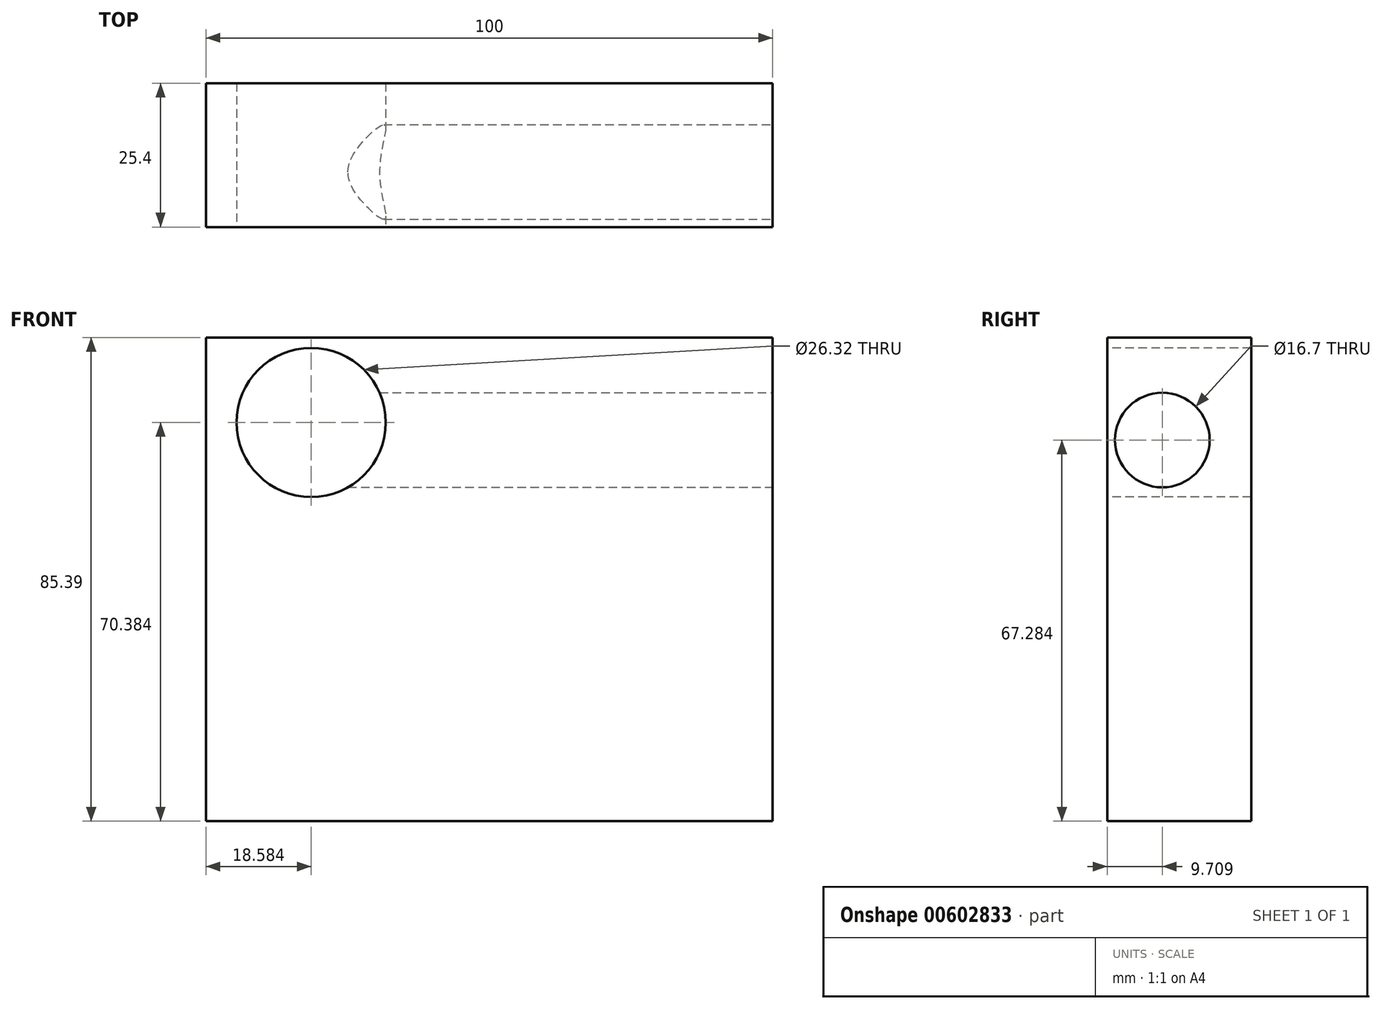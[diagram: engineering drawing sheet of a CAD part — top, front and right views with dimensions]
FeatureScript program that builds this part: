
annotation { "Feature Type Name" : "Feature", "Feature Type Description" : "" }
export const myFeature = defineFeature(function(context is Context, id is Id, definition is map)
    precondition{}
    {
        {
            var Q0;
            Q0=qCreatedBy(makeId("Front.planeOp"),FACE);
            var sketch = newSketch(context, id + "F0", { "sketchPlane" : qUnion([Q0])});
            skLineSegment(sketch, "E0.bottom", {"start": v(0, 0) * mm, "end": v(100, 0) * mm});
            skLineSegment(sketch, "E0.top", {"start": v(0, 85.4) * mm, "end": v(100, 85.4) * mm});
            skLineSegment(sketch, "E0.left", {"start": v(0, 0) * mm, "end": v(0, 85.4) * mm});
            skLineSegment(sketch, "E0.right", {"start": v(100, 0) * mm, "end": v(100, 85.4) * mm});
            skSolve(sketch);
        }
        {
            var Q0;
            Q0=makeQuery(id+"F0.imprint","IMPRINT",FACE,{"disambiguationData":[TD([[makeQuery(id+"F0.imprint","IMPRINT",EDGE,{"derivedFrom":sQuery(id+"F0.wireOp",EDGE,"E0.bottom")}),1.0]])]});
            extrude(context, id + "F1", {"entities" : qUnion([Q0]), "depth" : 25.4 * mm, "offsetDistance" : 25.4 * mm});
        }
        {
            var Q0;
            Q0=makeQuery(id+"F1.opExtrude","CAP_FACE",FACE,{"disambiguationData":[OSD([sQuery(id+"F0.wireOp",EDGE,"E0.bottom"),sQuery(id+"F0.wireOp",EDGE,"E0.top"),sQuery(id+"F0.wireOp",EDGE,"E0.left"),sQuery(id+"F0.wireOp",EDGE,"E0.right")])],"isStart":false});
            var sketch = newSketch(context, id + "F2", { "sketchPlane" : qUnion([Q0])});
            skCircle(sketch, "E1", {"center": v(18.58, 70.38) * mm, "radius": 13.16 * mm});
            skSolve(sketch);
        }
        {
            var Q0;
            Q0=makeQuery(id+"F2.imprint","IMPRINT",FACE,{"disambiguationData":[TD([[makeQuery(id+"F2.imprint","IMPRINT",EDGE,{"derivedFrom":sQuery(id+"F2.wireOp",EDGE,"E1")}),1.0]])]});
            extrude(context, id + "F3", {"entities" : qUnion([Q0]), "operationType" : NewBodyOperationType.REMOVE, "oppositeDirection" : true, "depth" : 25.4 * mm, "offsetDistance" : 25.4 * mm});
        }
        {
            var Q0;
            Q0=makeQuery(id+"F1.opExtrude","SWEPT_FACE",FACE,{"disambiguationData":[OSD([sQuery(id+"F0.wireOp",EDGE,"E0.right")])]});
            var sketch = newSketch(context, id + "F4", { "sketchPlane" : qUnion([Q0])});
            skCircle(sketch, "E2", {"center": v(-15.7, 67.28) * mm, "radius": 8.35 * mm});
            skSolve(sketch);
        }
        {
            var Q0;
            Q0 = qSketchRegion(id + "F4", true);
            extrude(context, id + "F5", {"entities" : qUnion([Q0]), "operationType" : NewBodyOperationType.REMOVE, "oppositeDirection" : true, "depth" : 25.4 * mm, "offsetDistance" : 25.4 * mm});
        }
        {
            var Q0;
            Q0=makeQuery(id+"F5.boolean.opBoolean","COPY",FACE,{"derivedFrom":makeQuery(id+"F5.opExtrude","CAP_FACE",FACE,{"disambiguationData":[OSD([sQuery(id+"F4.wireOp",EDGE,"E2")])],"isStart":false})});
            extrude(context, id + "F6", {"entities" : qUnion([Q0]), "operationType" : NewBodyOperationType.REMOVE, "oppositeDirection" : true, "depth" : 25.4 * mm, "offsetDistance" : 25.4 * mm});
        }
        {
            var Q0;
            Q0=makeQuery(id+"F6.boolean.opBoolean","COPY",FACE,{"derivedFrom":makeQuery(id+"F6.opExtrude","CAP_FACE",FACE,{"disambiguationData":[OSD([sQuery(id+"F4.wireOp",EDGE,"E2")])],"isStart":false})});
            extrude(context, id + "F7", {"entities" : qUnion([Q0]), "operationType" : NewBodyOperationType.REMOVE, "oppositeDirection" : true, "depth" : 25.4 * mm, "offsetDistance" : 25.4 * mm});
        }
    });
